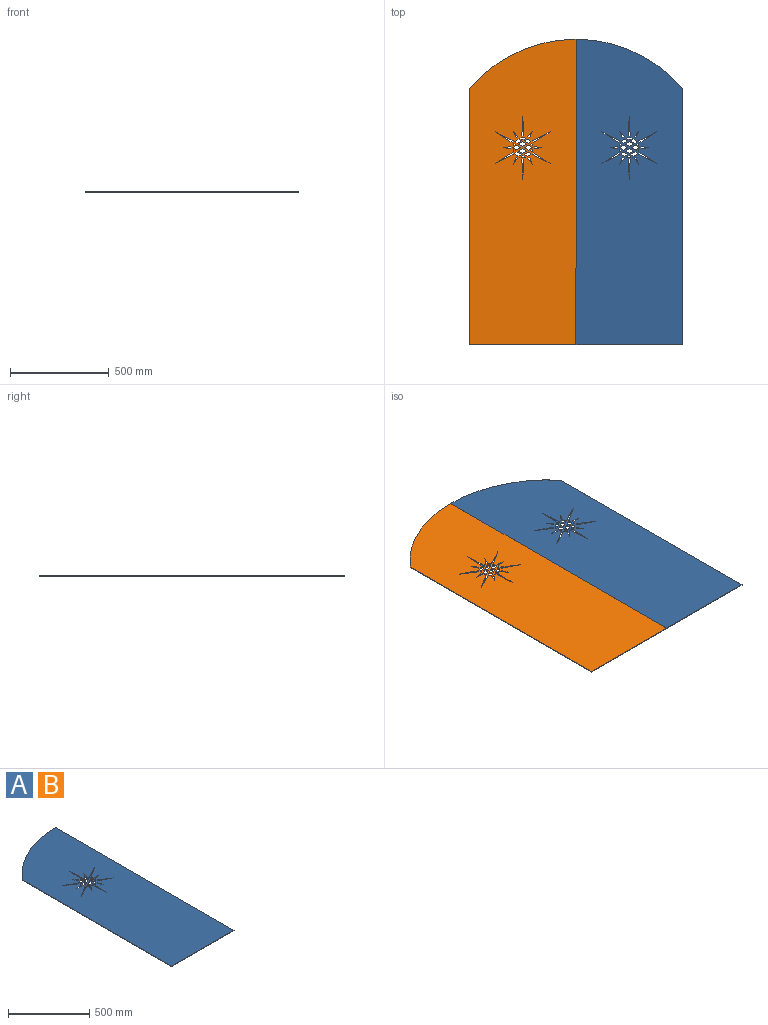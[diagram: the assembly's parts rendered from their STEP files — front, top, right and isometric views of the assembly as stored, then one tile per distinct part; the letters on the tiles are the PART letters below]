
ASSEMBLY  parts=2 mates=1
PART A: 92 faces, bbox 540x1550x3 mm
  f0: plane 84.1x54.33mm, normal (0.54,0.84,0), area 300.4mm2, adj f1,f89,f90,f91
  f1: plane 89.1x45.67mm, normal (-0.46,-0.89,0), area 300.4mm2, adj f0,f89,f90,f91
  f2: plane 89.1x45.67mm, normal (-0.46,0.89,0), area 300.4mm2, adj f3,f63,f90,f91
  f3: plane 84.1x54.33mm, normal (0.54,-0.84,0), area 300.4mm2, adj f2,f63,f90,f91
  f4: plane 100x5mm, normal (-1,0.05,0), area 300.4mm2, adj f5,f64,f90,f91
  f5: plane 100x5mm, normal (1,0.05,0), area 300.4mm2, adj f4,f64,f90,f91
  f6: plane 84.1x54.33mm, normal (-0.54,-0.84,0), area 300.4mm2, adj f7,f65,f90,f91
  f7: plane 89.1x45.67mm, normal (0.46,0.89,0), area 300.4mm2, adj f6,f65,f90,f91
  f8: plane 89.1x45.67mm, normal (0.46,-0.89,0), area 300.4mm2, adj f9,f66,f90,f91
  f9: plane 84.1x54.33mm, normal (-0.54,0.84,0), area 300.4mm2, adj f8,f66,f90,f91
  f10: plane 8.66x5mm, normal (0.5,0.87,0), area 30mm2, adj f11,f67,f90,f91
  f11: plane 29.12x22.59mm, normal (0.79,-0.61,0), area 110.6mm2, adj f10,f67,f90,f91
  f12: plane 20.67x11.93mm, normal (-0.5,-0.87,0), area 71.6mm2, adj f13,f68,f90,f91
  f13: plane 20.67x11.93mm, normal (-0.5,0.87,0), area 71.6mm2, adj f12,f14,f90,f91
  f14: plane 20.67x11.93mm, normal (0.5,0.87,0), area 71.6mm2, adj f13,f68,f90,f91
  f15: plane 11.25x6.5mm, normal (0.5,-0.87,0), area 39mm2, adj f16,f69,f90,f91
  f16: plane 20.67x11.93mm, normal (-0.5,-0.87,0), area 71.6mm2, adj f15,f17,f90,f91
  f17: plane 15.66x9.04mm, normal (-0.5,0.87,0), area 54.3mm2, adj f16,f69,f90,f91
  f18: plane 20.64x11.95mm, normal (0.5,0.87,0), area 71.5mm2, adj f19,f70,f90,f91
  f19: plane 20.58x11.88mm, normal (0.5,-0.87,0), area 71.3mm2, adj f18,f20,f90,f91
  f20: plane 20.67x11.93mm, normal (-0.5,-0.87,0), area 71.6mm2, adj f19,f70,f90,f91
  f21: plane 9.32x5.38mm, normal (0.5,0.87,0), area 32.3mm2, adj f22,f71,f90,f91
  f22: plane 6.25x3.61mm, normal (0.5,-0.87,0), area 21.7mm2, adj f21,f71,f90,f91
  f23: plane 9.32x5.38mm, normal (0.5,-0.87,0), area 32.3mm2, adj f24,f72,f90,f91
  f24: cylinder r=50mm len=8.99mm, axis (0,0,-1), area 28.5mm2, adj f23,f72,f90,f91
  f25: plane 11.25x6.5mm, normal (-0.5,-0.87,0), area 39mm2, adj f26,f73,f90,f91
  f26: cylinder r=50mm len=16.24mm, axis (0,0,-1), area 65.8mm2, adj f25,f27,f90,f91
  f27: plane 15.64x9.06mm, normal (0.5,0.87,0), area 54.2mm2, adj f26,f73,f90,f91
  f28: plane 14.32x8.27mm, normal (0.5,-0.87,0), area 49.6mm2, adj f29,f74,f90,f91
  f29: plane 14.32x8.27mm, normal (-0.5,-0.87,0), area 49.6mm2, adj f28,f74,f90,f91
  f30: plane 6.25x3.61mm, normal (-0.5,0.87,0), area 21.7mm2, adj f31,f75,f90,f91
  f31: cylinder r=50mm len=8.99mm, axis (0,0,-1), area 28.5mm2, adj f30,f75,f90,f91
  f32: plane 20.64x11.95mm, normal (0.5,0.87,0), area 71.5mm2, adj f33,f76,f90,f91
  f33: plane 20.53x11.85mm, normal (0.5,-0.87,0), area 71.1mm2, adj f32,f34,f90,f91
  f34: plane 20.67x11.93mm, normal (-0.5,-0.87,0), area 71.6mm2, adj f33,f76,f90,f91
  f35: plane 9.32x5.38mm, normal (-0.5,0.87,0), area 32.3mm2, adj f36,f77,f90,f91
  f36: cylinder r=50mm len=8.99mm, axis (0,0,-1), area 28.5mm2, adj f35,f77,f90,f91
  f37: plane 20.67x11.93mm, normal (-0.5,0.87,0), area 71.6mm2, adj f38,f78,f90,f91
  f38: plane 11.25x6.5mm, normal (0.5,0.87,0), area 39mm2, adj f37,f39,f90,f91
  f39: cylinder r=50mm len=16.26mm, axis (0,0,-1), area 65.8mm2, adj f38,f78,f90,f91
  f40: plane 14.32x8.27mm, normal (0.5,0.87,0), area 49.6mm2, adj f41,f79,f90,f91
  f41: cylinder r=50mm len=28.63mm, axis (0,0,-1), area 87.1mm2, adj f40,f79,f90,f91
  f42: plane 20.67x11.93mm, normal (0.5,-0.87,0), area 71.6mm2, adj f43,f80,f90,f91
  f43: plane 20.67x11.93mm, normal (-0.5,-0.87,0), area 71.6mm2, adj f42,f44,f90,f91
  f44: plane 20.67x11.93mm, normal (-0.5,0.87,0), area 71.6mm2, adj f43,f80,f90,f91
  f45: cylinder r=50mm len=16.26mm, axis (0,0,-1), area 65.8mm2, adj f46,f81,f90,f91
  f46: plane 11.25x6.5mm, normal (-0.5,0.87,0), area 39mm2, adj f45,f47,f90,f91
  f47: plane 20.67x11.93mm, normal (0.5,0.87,0), area 71.6mm2, adj f46,f81,f90,f91
  f48: plane 1300x3mm, normal (-1,0,0), area 3900mm2, adj f49,f82,f90,f91
  f49: plane 540x3mm, normal (0,-1,0), area 1620mm2, adj f48,f50,f90,f91
  f50: plane 1550x3mm, normal (1,0,0), area 4650mm2, adj f49,f82,f90,f91
  f51: plane 36.51x5mm, normal (-0.14,0.99,0), area 110.6mm2, adj f52,f83,f90,f91
  f52: plane 10x3mm, normal (1,0,0), area 30mm2, adj f51,f83,f90,f91
  f53: plane 29.12x22.59mm, normal (0.79,0.61,0), area 110.6mm2, adj f54,f84,f90,f91
  f54: plane 8.66x5mm, normal (0.5,-0.87,0), area 30mm2, adj f53,f84,f90,f91
  f55: plane 34.12x13.93mm, normal (0.93,-0.38,0), area 110.6mm2, adj f56,f85,f90,f91
  f56: plane 8.66x5mm, normal (-0.5,-0.87,0), area 30mm2, adj f55,f85,f90,f91
  f57: plane 36.51x5mm, normal (0.14,-0.99,0), area 110.6mm2, adj f58,f86,f90,f91
  f58: plane 10x3mm, normal (-1,0,0), area 30mm2, adj f57,f86,f90,f91
  f59: plane 29.12x22.59mm, normal (-0.79,-0.61,0), area 110.6mm2, adj f60,f87,f90,f91
  f60: plane 8.66x5mm, normal (-0.5,0.87,0), area 30mm2, adj f59,f87,f90,f91
  f61: plane 10x3mm, normal (0,1,0), area 30mm2, adj f62,f88,f90,f91
  f62: plane 100x5mm, normal (1,-0.05,0), area 300.4mm2, adj f61,f88,f90,f91
  f63: plane 8.66x5mm, normal (-0.87,-0.5,0), area 30mm2, adj f2,f3,f90,f91
  f64: plane 10x3mm, normal (0,-1,0), area 30mm2, adj f4,f5,f90,f91
  f65: plane 8.66x5mm, normal (0.87,-0.5,0), area 30mm2, adj f6,f7,f90,f91
  f66: plane 8.66x5mm, normal (0.87,0.5,0), area 30mm2, adj f8,f9,f90,f91
  f67: plane 34.12x13.93mm, normal (-0.93,0.38,0), area 110.6mm2, adj f10,f11,f90,f91
  f68: plane 20.67x11.93mm, normal (0.5,-0.87,0), area 71.6mm2, adj f12,f14,f90,f91
  f69: cylinder r=50mm len=16.26mm, axis (0,0,-1), area 65.8mm2, adj f15,f17,f90,f91
  f70: plane 20.61x11.9mm, normal (-0.5,0.87,0), area 71.4mm2, adj f18,f20,f90,f91
  f71: cylinder r=50mm len=8.99mm, axis (0,0,-1), area 28.5mm2, adj f21,f22,f90,f91
  f72: plane 6.25x3.61mm, normal (0.5,0.87,0), area 21.7mm2, adj f23,f24,f90,f91
  f73: plane 20.63x11.91mm, normal (0.5,-0.87,0), area 71.5mm2, adj f25,f27,f90,f91
  f74: cylinder r=50mm len=28.63mm, axis (0,0,-1), area 87.1mm2, adj f28,f29,f90,f91
  f75: plane 9.32x5.38mm, normal (-0.5,-0.87,0), area 32.3mm2, adj f30,f31,f90,f91
  f76: plane 20.56x11.87mm, normal (-0.5,0.87,0), area 71.2mm2, adj f32,f34,f90,f91
  f77: plane 6.25x3.61mm, normal (-0.5,-0.87,0), area 21.7mm2, adj f35,f36,f90,f91
  f78: plane 15.66x9.04mm, normal (-0.5,-0.87,0), area 54.3mm2, adj f37,f39,f90,f91
  f79: plane 14.32x8.27mm, normal (-0.5,0.87,0), area 49.6mm2, adj f40,f41,f90,f91
  f80: plane 20.67x11.93mm, normal (0.5,0.87,0), area 71.6mm2, adj f42,f44,f90,f91
  f81: plane 15.66x9.04mm, normal (0.5,-0.87,0), area 54.3mm2, adj f45,f47,f90,f91
  f82: cylinder r=708.2mm len=540mm, axis (0,0,-1), area 1842.4mm2, adj f48,f50,f90,f91
  f83: plane 36.51x5mm, normal (-0.14,-0.99,0), area 110.6mm2, adj f51,f52,f90,f91
  f84: plane 34.12x13.93mm, normal (-0.93,-0.38,0), area 110.6mm2, adj f53,f54,f90,f91
  f85: plane 29.12x22.59mm, normal (-0.79,0.61,0), area 110.6mm2, adj f55,f56,f90,f91
  f86: plane 36.51x5mm, normal (0.14,0.99,0), area 110.6mm2, adj f57,f58,f90,f91
  f87: plane 34.12x13.93mm, normal (0.93,0.38,0), area 110.6mm2, adj f59,f60,f90,f91
  f88: plane 100x5mm, normal (-1,-0.05,0), area 300.4mm2, adj f61,f62,f90,f91
  f89: plane 8.66x5mm, normal (-0.87,0.5,0), area 30mm2, adj f0,f1,f90,f91
  f90: plane 1550x540mm, normal (0,0,1), area 787872.1mm2, adj f0,f1,f2,f3,f4,f5,f6,f7
  f91: plane 1550x540mm, normal (0,0,-1), area 787872.1mm2, adj f0,f1,f2,f3,f4,f5,f6,f7
PART B: same geometry as A
PLACE A rot(axis=(0,1,0),180deg) t=(1044.61,137.69,-275.3)mm
PLACE B t=(1044.61,137.69,-278.3)mm
MATE fastened A.f50 <-> B.f50  axis (-1,0,0) through (1044.61,-512.31,-278.3)mm
